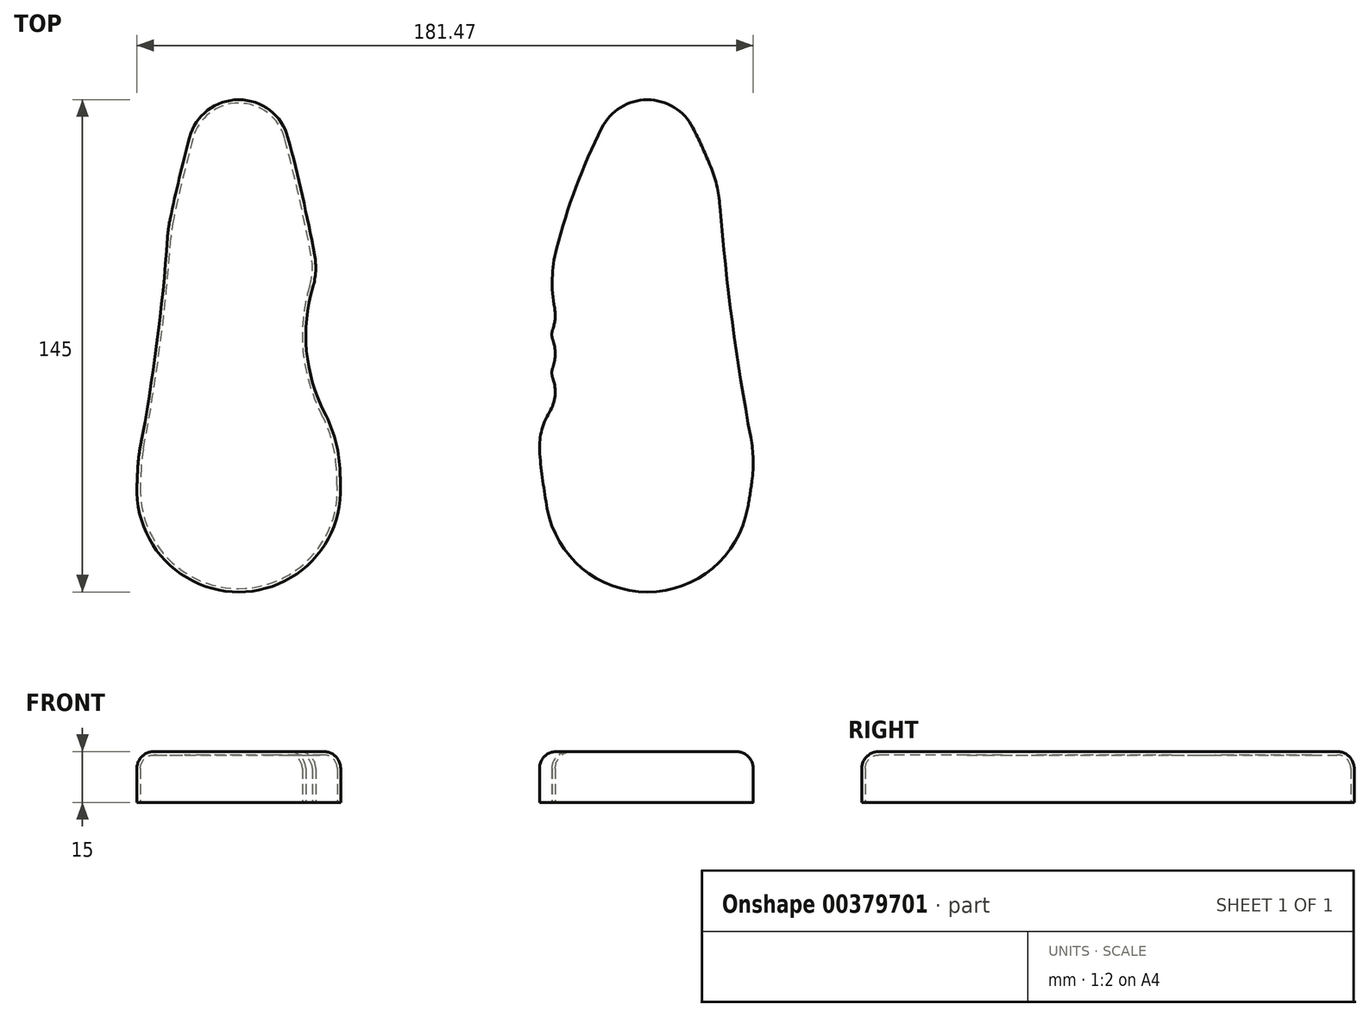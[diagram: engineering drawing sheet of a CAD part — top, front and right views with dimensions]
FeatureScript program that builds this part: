
annotation { "Feature Type Name" : "Feature", "Feature Type Description" : "" }
export const myFeature = defineFeature(function(context is Context, id is Id, definition is map)
    precondition{}
    {
        {
            var Q0;
            Q0=qCreatedBy(makeId("Top.planeOp"),FACE);
            var sketch = newSketch(context, id + "F0", { "sketchPlane" : qUnion([Q0])});
            skArc(sketch, "E0", {"start": v(14.5, 46.76) * mm, "mid": v(0, 57.9) * mm, "end": v(-14.5, 46.76) * mm});
            skArc(sketch, "E1", {"start": v(-29.98, -55.93) * mm, "mid": v(0, -87.1) * mm, "end": v(29.98, -55.93) * mm});
            skArc(sketch, "E2", {"start": v(-14.5, 46.76) * mm, "mid": v(-17.52, 34.77) * mm, "end": v(-20.23, 22.71) * mm});
            skArc(sketch, "E3.MirrorCS", {"start": v(14.5, 46.76) * mm, "mid": v(18.74, 29.52) * mm, "end": v(22.33, 12.13) * mm});
            skArc(sketch, "E4", {"start": v(21.82, 2.7) * mm, "mid": v(19.94, -16.14) * mm, "end": v(25.29, -34.3) * mm});
            skArc(sketch, "E5.trimOffspring", {"start": v(29.75, -50.74) * mm, "mid": v(29.87, -53.33) * mm, "end": v(29.98, -55.93) * mm});
            skPoint(sketch, "E6.visualSharp", {"position": v(29.12, -40.5) * mm});
            skArc(sketch, "E6.filletArc", {"start": v(29.75, -50.74) * mm, "mid": v(28.4, -42.28) * mm, "end": v(25.29, -34.3) * mm});
            skPoint(sketch, "E7.visualSharp", {"position": v(23.28, 6.87) * mm});
            skArc(sketch, "E7.filletArc", {"start": v(21.82, 2.7) * mm, "mid": v(22.64, 7.38) * mm, "end": v(22.33, 12.13) * mm});
            skArc(sketch, "E8", {"start": v(-29.07, -44.8) * mm, "mid": v(-24.11, -13.88) * mm, "end": v(-20.98, 17.29) * mm});
            skArc(sketch, "E9.trimOffspring", {"start": v(-29.72, -50.24) * mm, "mid": v(-29.86, -53.08) * mm, "end": v(-29.98, -55.93) * mm});
            skPoint(sketch, "E10.visualSharp", {"position": v(-20.8, 19.92) * mm});
            skArc(sketch, "E10.filletArc", {"start": v(-20.23, 22.71) * mm, "mid": v(-20.7, 20.01) * mm, "end": v(-20.98, 17.29) * mm});
            skPoint(sketch, "E11.visualSharp", {"position": v(-29.57, -47.4) * mm});
            skArc(sketch, "E11.filletArc", {"start": v(-29.07, -44.8) * mm, "mid": v(-29.49, -47.51) * mm, "end": v(-29.72, -50.24) * mm});
            skSolve(sketch);
        }
        {
            var Q0;
            Q0=makeQuery(id+"F0.imprint","IMPRINT",FACE,{"disambiguationData":[TD([[makeQuery(id+"F0.imprint","IMPRINT",EDGE,{"derivedFrom":sQuery(id+"F0.wireOp",EDGE,"E0")}),1.0]])]});
            extrude(context, id + "F1", {"entities" : qUnion([Q0]), "depth" : 15 * mm});
        }
        {
            var Q0;
            Q0=makeQuery(id+"F1.opExtrude","CAP_EDGE",EDGE,{"disambiguationData":[OSD([sQuery(id+"F0.wireOp",EDGE,"E1")])],"isStart":false});
            fillet(context, id + "F2", {"entities" : qUnion([Q0]), "radius" : 5 * mm, "tangentPropagation" : true, "allowEdgeOverflow" : false});
        }
        {
            var Q0;
            Q0=makeQuery(id+"F1.opExtrude","CAP_FACE",FACE,{"disambiguationData":[OSD([sQuery(id+"F0.wireOp",EDGE,"E0"),sQuery(id+"F0.wireOp",EDGE,"E1"),sQuery(id+"F0.wireOp",EDGE,"E2"),sQuery(id+"F0.wireOp",EDGE,"E3.MirrorCS"),sQuery(id+"F0.wireOp",EDGE,"E4"),sQuery(id+"F0.wireOp",EDGE,"E5.trimOffspring"),sQuery(id+"F0.wireOp",EDGE,"E6.filletArc"),sQuery(id+"F0.wireOp",EDGE,"E7.filletArc"),sQuery(id+"F0.wireOp",EDGE,"E8"),sQuery(id+"F0.wireOp",EDGE,"E9.trimOffspring"),sQuery(id+"F0.wireOp",EDGE,"E10.filletArc"),sQuery(id+"F0.wireOp",EDGE,"E11.filletArc")])],"isStart":true});
            shell(context, id + "F3", {"entities" : qUnion([Q0]), "thickness" : 1 * mm});
        }
        {
            var Q0;
            Q0=qCreatedBy(makeId("Top.planeOp"),FACE);
            var sketch = newSketch(context, id + "F4", { "sketchPlane" : qUnion([Q0])});
            skArc(sketch, "E12.0", {"start": v(9.66, 45.47) * mm, "mid": v(0, 52.9) * mm, "end": v(-9.66, 45.47) * mm});
            skLineSegment(sketch, "E13.0.0", {"start": v(-24.98, -56.12) * mm, "end": v(-29.98, -55.93) * mm});
            skArc(sketch, "E13.0.1", {"start": v(29.98, -55.93) * mm, "mid": v(0, -87.1) * mm, "end": v(-29.98, -55.93) * mm});
            skLineSegment(sketch, "E13.0.2", {"start": v(29.98, -55.93) * mm, "end": v(24.98, -56.12) * mm});
            skArc(sketch, "E13.0.3", {"start": v(24.98, -56.12) * mm, "mid": v(0, -82.1) * mm, "end": v(-24.98, -56.12) * mm});
            skArc(sketch, "E14", {"start": v(133.73, 49.63) * mm, "mid": v(120.32, 57.9) * mm, "end": v(106.92, 49.63) * mm});
            skArc(sketch, "E15", {"start": v(90.8, -62.46) * mm, "mid": v(120.32, -87.1) * mm, "end": v(149.84, -62.46) * mm});
            skArc(sketch, "E16", {"start": v(106.92, 49.63) * mm, "mid": v(99.28, 32.14) * mm, "end": v(93.55, 13.93) * mm});
            skLineSegment(sketch, "E17", {"start": v(120.32, 76.08) * mm, "end": v(120.32, -101.85) * mm, "construction": true});
            skArc(sketch, "E18.MirrorCS", {"start": v(133.73, 49.63) * mm, "mid": v(136.3, 44.3) * mm, "end": v(138.69, 38.88) * mm});
            skArc(sketch, "E19.trimOffspring", {"start": v(88.63, -46.34) * mm, "mid": v(89.53, -54.42) * mm, "end": v(90.8, -62.46) * mm});
            skArc(sketch, "E20.trimOffspring", {"start": v(91.68, -11.25) * mm, "mid": v(93.04, -7.5) * mm, "end": v(93, -3.5) * mm});
            skArc(sketch, "E21.trimOffspring", {"start": v(91.68, -22.53) * mm, "mid": v(93.2, -16.9) * mm, "end": v(91.68, -11.25) * mm});
            skArc(sketch, "E22.trimOffspring", {"start": v(91.52, -34.08) * mm, "mid": v(93.2, -28.33) * mm, "end": v(91.68, -22.53) * mm});
            skPoint(sketch, "E23.visualSharp", {"position": v(90.8, 1.34) * mm});
            skArc(sketch, "E23.filletArc", {"start": v(93.55, 13.93) * mm, "mid": v(92.31, 5.25) * mm, "end": v(93, -3.5) * mm});
            skPoint(sketch, "E24.visualSharp", {"position": v(88.07, -37.62) * mm});
            skArc(sketch, "E24.filletArc", {"start": v(91.52, -34.08) * mm, "mid": v(89.09, -39.98) * mm, "end": v(88.63, -46.34) * mm});
            skArc(sketch, "E25", {"start": v(141.7, 26.5) * mm, "mid": v(145.34, -7.7) * mm, "end": v(150.79, -41.67) * mm});
            skArc(sketch, "E26.trimOffspring", {"start": v(151.12, -54.4) * mm, "mid": v(150.52, -58.43) * mm, "end": v(149.84, -62.46) * mm});
            skPoint(sketch, "E27.visualSharp", {"position": v(141.26, 32.43) * mm});
            skArc(sketch, "E27.filletArc", {"start": v(141.7, 26.5) * mm, "mid": v(140.7, 32.81) * mm, "end": v(138.69, 38.88) * mm});
            skPoint(sketch, "E28.visualSharp", {"position": v(151.9, -47.5) * mm});
            skArc(sketch, "E28.filletArc", {"start": v(151.12, -54.4) * mm, "mid": v(151.46, -48.02) * mm, "end": v(150.79, -41.67) * mm});
            skSolve(sketch);
        }
        {
            var Q0;
            Q0=makeQuery(id+"F4.imprint","IMPRINT",FACE,{"disambiguationData":[TD([[makeQuery(id+"F4.imprint","IMPRINT",EDGE,{"derivedFrom":sQuery(id+"F4.wireOp",EDGE,"E14")}),1.0]])]});
            extrude(context, id + "F5", {"entities" : qUnion([Q0]), "depth" : 15 * mm});
        }
        {
            var Q0;
            Q0=makeQuery(id+"F5.opExtrude","SWEPT_EDGE",EDGE,{"disambiguationData":[OSD([sQuery(id+"F4.wireOp",EDGE,"E20.trimOffspring"),sQuery(id+"F4.wireOp",EDGE,"E21.trimOffspring")])]});
            fillet(context, id + "F6", {"entities" : qUnion([Q0]), "radius" : 5 * mm, "tangentPropagation" : true, "allowEdgeOverflow" : false});
        }
        {
            var Q0;
            Q0=makeQuery(id+"F5.opExtrude","SWEPT_EDGE",EDGE,{"disambiguationData":[OSD([sQuery(id+"F4.wireOp",EDGE,"E21.trimOffspring"),sQuery(id+"F4.wireOp",EDGE,"E22.trimOffspring")])]});
            fillet(context, id + "F7", {"entities" : qUnion([Q0]), "radius" : 5 * mm, "tangentPropagation" : true, "allowEdgeOverflow" : false});
        }
        {
            var Q0;
            Q0=makeQuery(id+"F5.opExtrude","CAP_EDGE",EDGE,{"disambiguationData":[OSD([sQuery(id+"F4.wireOp",EDGE,"E23.filletArc")])],"isStart":false});
            fillet(context, id + "F8", {"entities" : qUnion([Q0]), "radius" : 5 * mm, "tangentPropagation" : true, "allowEdgeOverflow" : false});
        }
    });
